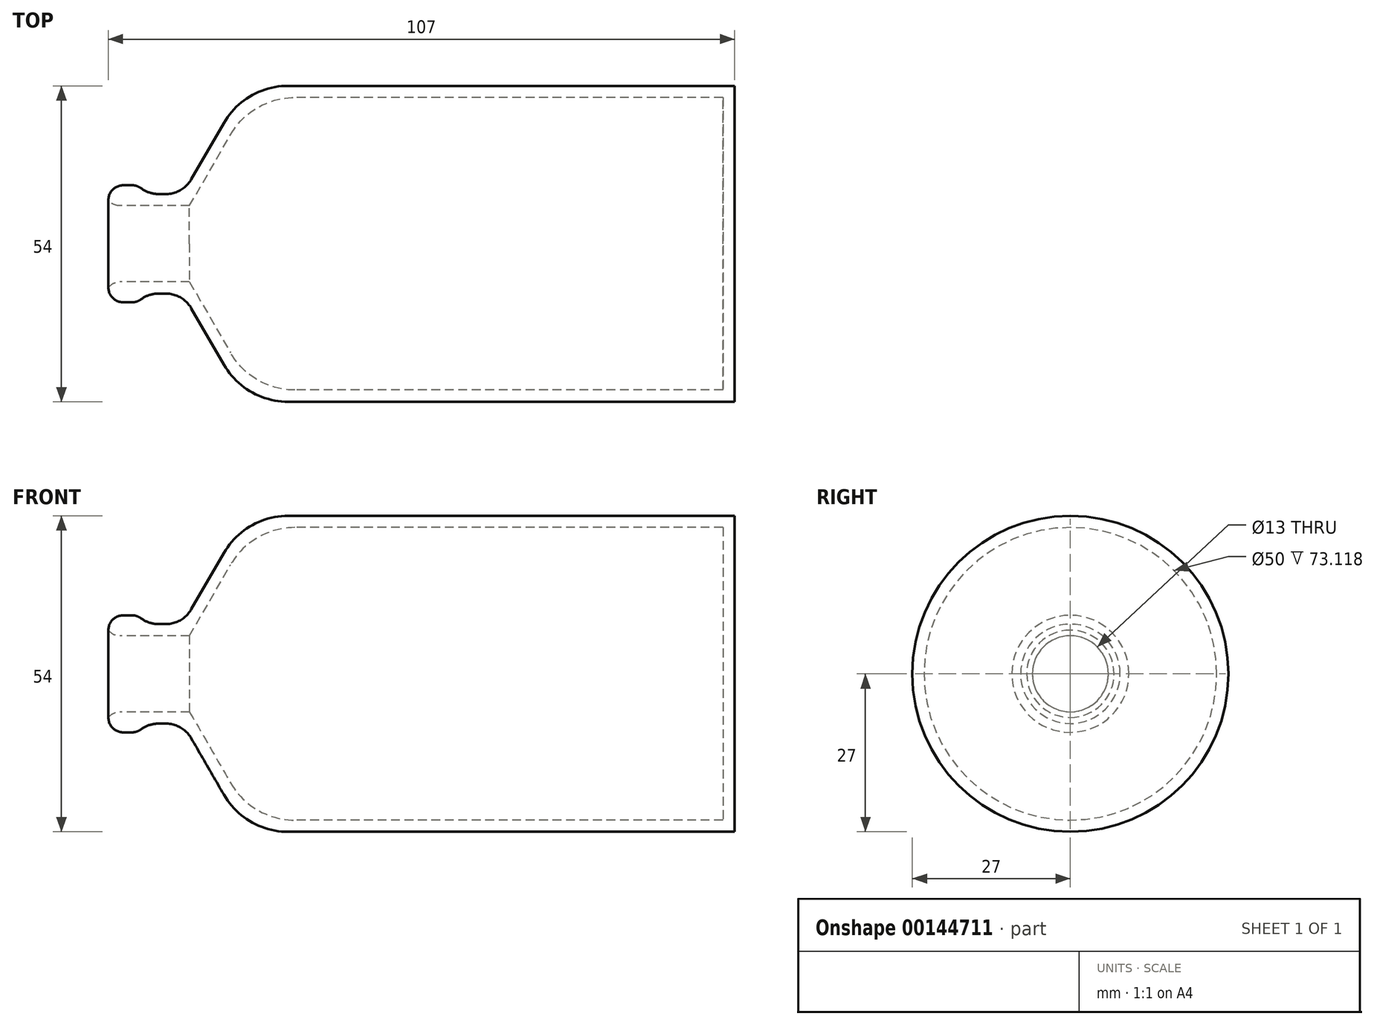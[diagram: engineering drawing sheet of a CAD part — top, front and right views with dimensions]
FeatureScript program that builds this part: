
annotation { "Feature Type Name" : "Feature", "Feature Type Description" : "" }
export const myFeature = defineFeature(function(context is Context, id is Id, definition is map)
    precondition{}
    {
        {
            var Q0;
            Q0=qCreatedBy(makeId("Front.planeOp"),FACE);
            var sketch = newSketch(context, id + "F0", { "sketchPlane" : qUnion([Q0])});
            skLineSegment(sketch, "E0", {"start": v(-53.5, 0) * mm, "end": v(53.5, 0) * mm, "construction": true});
            skLineSegment(sketch, "E1", {"start": v(-30.1, 27) * mm, "end": v(53.5, 27) * mm});
            skLineSegment(sketch, "E2", {"start": v(-53.5, 10) * mm, "end": v(-48.5, 10) * mm});
            skLineSegment(sketch, "E3", {"start": v(-53.5, 6.5) * mm, "end": v(-39.63, 6.5) * mm});
            skLineSegment(sketch, "E4", {"start": v(51.5, 25) * mm, "end": v(-28.95, 25) * mm});
            skLineSegment(sketch, "E5", {"start": v(-28.95, 25) * mm, "end": v(-39.63, 6.5) * mm});
            skLineSegment(sketch, "E6", {"start": v(-48.5, 10) * mm, "end": v(-48.5, 8.5) * mm});
            skLineSegment(sketch, "E7", {"start": v(-48.5, 8.5) * mm, "end": v(-40.79, 8.5) * mm});
            skLineSegment(sketch, "E8", {"start": v(-40.79, 8.5) * mm, "end": v(-30.1, 27) * mm});
            skPoint(sketch, "E9.orphan", {"position": v(-53.5, 27) * mm});
            skLineSegment(sketch, "E10", {"start": v(53.5, 27) * mm, "end": v(53.5, 0) * mm});
            skLineSegment(sketch, "E11", {"start": v(51.5, 25) * mm, "end": v(51.5, 0) * mm});
            skPoint(sketch, "E12.orphan", {"position": v(53.5, 25) * mm});
            skLineSegment(sketch, "E13", {"start": v(-53.5, 10) * mm, "end": v(-53.5, 6.5) * mm});
            skLineSegment(sketch, "E14", {"start": v(51.5, 0) * mm, "end": v(53.5, 0) * mm});
            skSolve(sketch);
        }
        {
            var Q0;
            Q0 = qSketchRegion(id + "F0", true);
            var Q1;
            Q1=sQuery(id+"F0.wireOp",EDGE,"E0");
            revolve(context, id + "F1", {"entities" : qUnion([Q0]), "axis" : qUnion([Q1]), "revolveType" : RevolveType.FULL});
        }
        {
            var Q0;
            Q0=makeQuery(id+"F1.opRevolve","SWEPT_EDGE",EDGE,{"disambiguationData":[OSD([sQuery(id+"F0.wireOp",EDGE,"E1"),sQuery(id+"F0.wireOp",EDGE,"E8")])]});
            var Q1;
            Q1=makeQuery(id+"F1.opRevolve","SWEPT_EDGE",EDGE,{"disambiguationData":[OSD([sQuery(id+"F0.wireOp",EDGE,"E4"),sQuery(id+"F0.wireOp",EDGE,"E5")])]});
            fillet(context, id + "F2", {"entities" : qUnion([Q0, Q1]), "radius" : 12.7 * mm, "tangentPropagation" : true, "allowEdgeOverflow" : false});
        }
        {
            var Q0;
            Q0=makeQuery(id+"F1.opRevolve","SWEPT_EDGE",EDGE,{"disambiguationData":[OSD([sQuery(id+"F0.wireOp",EDGE,"E7"),sQuery(id+"F0.wireOp",EDGE,"E8")])]});
            var Q1;
            Q1=makeQuery(id+"F1.opRevolve","SWEPT_EDGE",EDGE,{"disambiguationData":[OSD([sQuery(id+"F0.wireOp",EDGE,"E6"),sQuery(id+"F0.wireOp",EDGE,"E7")])]});
            fillet(context, id + "F3", {"entities" : qUnion([Q0, Q1]), "radius" : 5.08 * mm, "tangentPropagation" : true, "allowEdgeOverflow" : false});
        }
        {
            var Q0;
            Q0=makeQuery(id+"F3.opFillet","BLEND_EDGE",EDGE,{"blendedFrom":[makeQuery(id+"F1.opRevolve","SWEPT_EDGE",EDGE,{"disambiguationData":[OSD([sQuery(id+"F0.wireOp",EDGE,"E6"),sQuery(id+"F0.wireOp",EDGE,"E7")])]}),makeQuery(id+"F1.opRevolve","SWEPT_FACE",FACE,{"disambiguationData":[OSD([sQuery(id+"F0.wireOp",EDGE,"E2")])]})],"blendedInto":[makeQuery(id+"F1.opRevolve","SWEPT_FACE",FACE,{"disambiguationData":[OSD([sQuery(id+"F0.wireOp",EDGE,"E2")])]})]});
            var Q1;
            Q1=makeQuery(id+"F1.opRevolve","SWEPT_EDGE",EDGE,{"disambiguationData":[OSD([sQuery(id+"F0.wireOp",EDGE,"E2"),sQuery(id+"F0.wireOp",EDGE,"E13")])]});
            fillet(context, id + "F4", {"entities" : qUnion([Q0, Q1]), "radius" : 2.54 * mm, "tangentPropagation" : true, "allowEdgeOverflow" : false});
        }
        {
            var Q0;
            Q0=makeQuery(id+"F1.opRevolve","SWEPT_EDGE",EDGE,{"disambiguationData":[OSD([sQuery(id+"F0.wireOp",EDGE,"E3"),sQuery(id+"F0.wireOp",EDGE,"E13")])]});
            fillet(context, id + "F5", {"entities" : qUnion([Q0]), "radius" : 2.54 * mm, "tangentPropagation" : true, "allowEdgeOverflow" : false});
        }
    });
